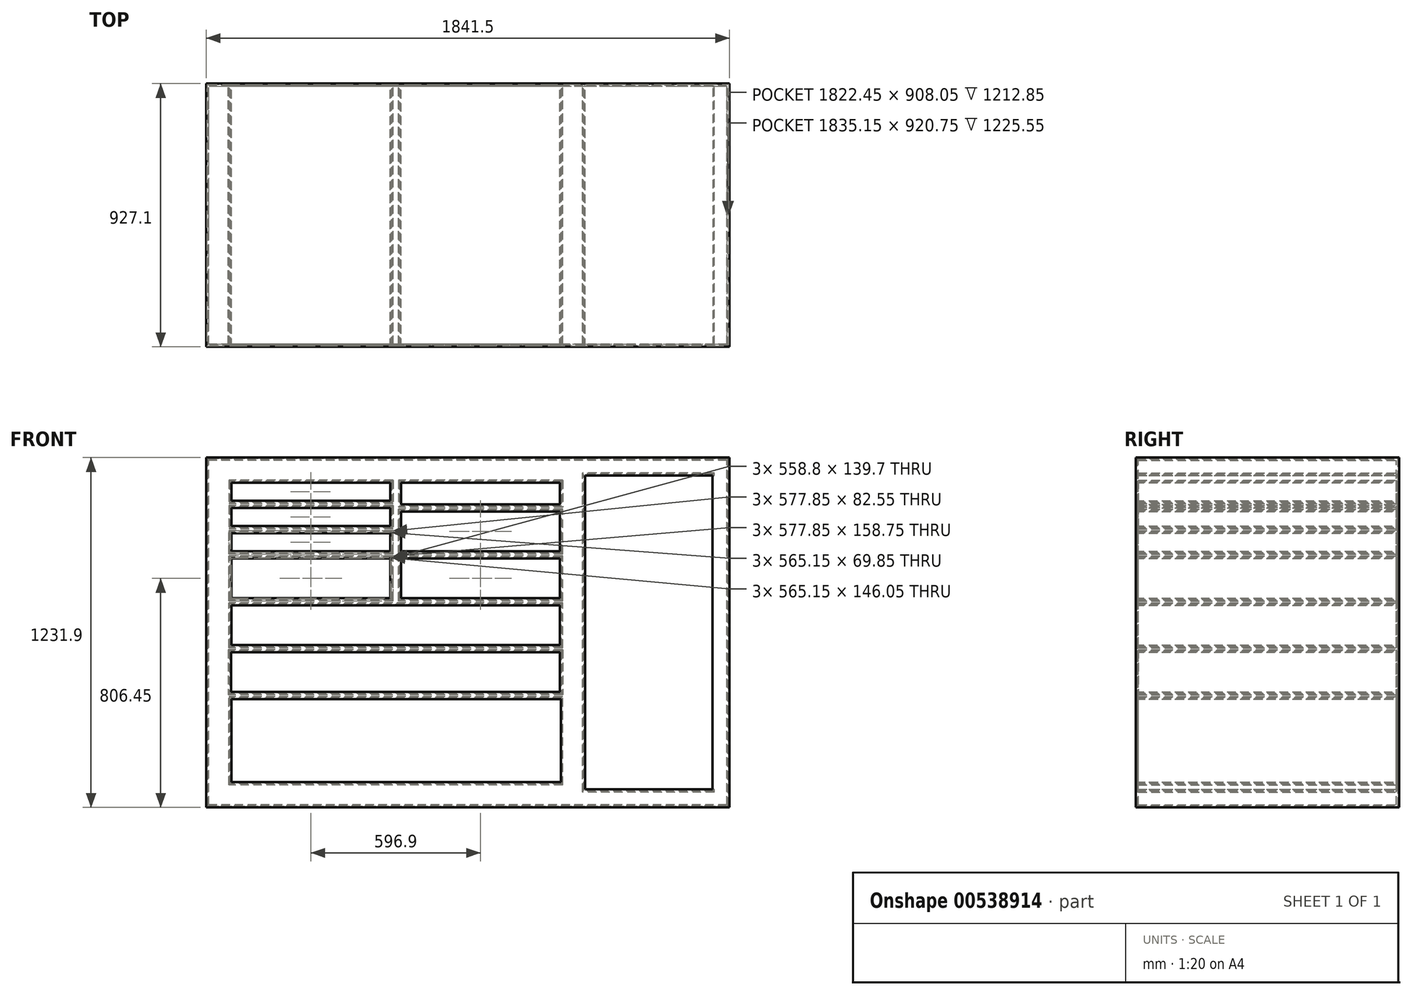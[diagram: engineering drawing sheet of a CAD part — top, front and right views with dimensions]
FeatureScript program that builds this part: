
annotation { "Feature Type Name" : "Feature", "Feature Type Description" : "" }
export const myFeature = defineFeature(function(context is Context, id is Id, definition is map)
    precondition{}
    {
        {
            var Q0;
            Q0=qCreatedBy(makeId("Front.planeOp"),FACE);
            var sketch = newSketch(context, id + "F0", { "sketchPlane" : qUnion([Q0])});
            skLineSegment(sketch, "E0.bottom", {"start": v(914.4, -609.6) * mm, "end": v(-914.4, -609.6) * mm});
            skLineSegment(sketch, "E0.top", {"start": v(914.4, 609.6) * mm, "end": v(-914.4, 609.6) * mm});
            skLineSegment(sketch, "E0.left", {"start": v(914.4, -609.6) * mm, "end": v(914.4, 609.6) * mm});
            skLineSegment(sketch, "E0.right", {"start": v(-914.4, -609.6) * mm, "end": v(-914.4, 609.6) * mm});
            skPoint(sketch, "E0.middle", {"position": v(0, 0) * mm});
            skPoint(sketch, "E1", {"position": v(635, 0) * mm});
            skLineSegment(sketch, "E2.bottom", {"start": v(863.6, -558.8) * mm, "end": v(406.4, -558.8) * mm});
            skLineSegment(sketch, "E2.top", {"start": v(863.6, 558.8) * mm, "end": v(406.4, 558.8) * mm});
            skLineSegment(sketch, "E2.left", {"start": v(863.6, -558.8) * mm, "end": v(863.6, 558.8) * mm});
            skLineSegment(sketch, "E2.right", {"start": v(406.4, -558.8) * mm, "end": v(406.4, 558.8) * mm});
            skPoint(sketch, "E3", {"position": v(-254, -381) * mm});
            skLineSegment(sketch, "E4.bottom", {"start": v(330.2, -533.4) * mm, "end": v(-838.2, -533.4) * mm});
            skLineSegment(sketch, "E4.top", {"start": v(330.2, -228.6) * mm, "end": v(-838.2, -228.6) * mm});
            skLineSegment(sketch, "E4.left", {"start": v(330.2, -533.4) * mm, "end": v(330.2, -228.6) * mm});
            skLineSegment(sketch, "E4.right", {"start": v(-838.2, -533.4) * mm, "end": v(-838.2, -228.6) * mm});
            skPoint(sketch, "E5", {"position": v(-254.77, -162.72) * mm});
            skPoint(sketch, "E6", {"position": v(-254.77, -139.7) * mm});
            skLineSegment(sketch, "E7.bottom", {"start": v(330.2, -63.5) * mm, "end": v(-839.75, -63.5) * mm});
            skLineSegment(sketch, "E7.top", {"start": v(330.2, -215.9) * mm, "end": v(-839.75, -215.9) * mm});
            skLineSegment(sketch, "E7.left", {"start": v(330.2, -63.5) * mm, "end": v(330.2, -215.9) * mm});
            skLineSegment(sketch, "E7.right", {"start": v(-839.75, -63.5) * mm, "end": v(-839.75, -215.9) * mm});
            skPoint(sketch, "E8", {"position": v(-254, 101.6) * mm});
            skPoint(sketch, "E9", {"position": v(-254, 266.7) * mm});
            skLineSegment(sketch, "E10.bottom", {"start": v(330.2, -50.8) * mm, "end": v(-838.2, -50.8) * mm});
            skLineSegment(sketch, "E10.top", {"start": v(330.2, 101.6) * mm, "end": v(-838.2, 101.6) * mm});
            skLineSegment(sketch, "E10.left", {"start": v(330.2, -50.8) * mm, "end": v(330.2, 101.6) * mm});
            skLineSegment(sketch, "E10.right", {"start": v(-838.2, -50.8) * mm, "end": v(-838.2, 101.6) * mm});
            skPoint(sketch, "E10.middle", {"position": v(-254, 78.58) * mm});
            skPoint(sketch, "E11", {"position": v(-584.2, 117.2) * mm});
            skPoint(sketch, "E12", {"position": v(44.45, 190.5) * mm});
            skPoint(sketch, "E13", {"position": v(-552.45, 317.5) * mm});
            skPoint(sketch, "E14", {"position": v(44.45, 355.6) * mm});
            skLineSegment(sketch, "E15.bottom", {"start": v(-266.7, 114.3) * mm, "end": v(-838.2, 114.3) * mm});
            skLineSegment(sketch, "E15.top", {"start": v(-266.7, 266.7) * mm, "end": v(-838.2, 266.7) * mm});
            skLineSegment(sketch, "E15.left", {"start": v(-266.7, 114.3) * mm, "end": v(-266.7, 266.7) * mm});
            skLineSegment(sketch, "E15.right", {"start": v(-838.2, 114.3) * mm, "end": v(-838.2, 266.7) * mm});
            skPoint(sketch, "E15.middle", {"position": v(-584.2, 238.8) * mm});
            skLineSegment(sketch, "E16.bottom", {"start": v(-266.7, 279.4) * mm, "end": v(-838.2, 279.4) * mm});
            skLineSegment(sketch, "E16.top", {"start": v(-266.7, 355.6) * mm, "end": v(-838.2, 355.6) * mm});
            skLineSegment(sketch, "E16.left", {"start": v(-266.7, 279.4) * mm, "end": v(-266.7, 355.6) * mm});
            skLineSegment(sketch, "E16.right", {"start": v(-838.2, 279.4) * mm, "end": v(-838.2, 355.6) * mm});
            skPoint(sketch, "E17", {"position": v(-552.45, 406.4) * mm});
            skPoint(sketch, "E17.positionSnap0", {"position": v(-552.45, 355.6) * mm});
            skLineSegment(sketch, "E18.bottom", {"start": v(-266.7, 444.5) * mm, "end": v(-838.2, 444.5) * mm});
            skLineSegment(sketch, "E18.top", {"start": v(-266.7, 368.3) * mm, "end": v(-838.2, 368.3) * mm});
            skLineSegment(sketch, "E18.left", {"start": v(-266.7, 444.5) * mm, "end": v(-266.7, 368.3) * mm});
            skLineSegment(sketch, "E18.right", {"start": v(-838.2, 444.5) * mm, "end": v(-838.2, 368.3) * mm});
            skPoint(sketch, "E19", {"position": v(-552.45, 495.3) * mm});
            skPoint(sketch, "E19.positionSnap0", {"position": v(-552.45, 444.5) * mm});
            skLineSegment(sketch, "E20.bottom", {"start": v(-266.7, 533.4) * mm, "end": v(-838.2, 533.4) * mm});
            skLineSegment(sketch, "E20.top", {"start": v(-266.7, 457.2) * mm, "end": v(-838.2, 457.2) * mm});
            skLineSegment(sketch, "E20.left", {"start": v(-266.7, 533.4) * mm, "end": v(-266.7, 457.2) * mm});
            skLineSegment(sketch, "E20.right", {"start": v(-838.2, 533.4) * mm, "end": v(-838.2, 457.2) * mm});
            skLineSegment(sketch, "E21.bottom", {"start": v(330.2, 114.3) * mm, "end": v(-241.3, 114.3) * mm});
            skLineSegment(sketch, "E21.top", {"start": v(330.2, 266.7) * mm, "end": v(-241.3, 266.7) * mm});
            skLineSegment(sketch, "E21.left", {"start": v(330.2, 114.3) * mm, "end": v(330.2, 266.7) * mm});
            skLineSegment(sketch, "E21.right", {"start": v(-241.3, 114.3) * mm, "end": v(-241.3, 266.7) * mm});
            skLineSegment(sketch, "E22.bottom", {"start": v(330.2, 279.4) * mm, "end": v(-241.3, 279.4) * mm});
            skLineSegment(sketch, "E22.top", {"start": v(330.2, 431.8) * mm, "end": v(-241.3, 431.8) * mm});
            skLineSegment(sketch, "E22.left", {"start": v(330.2, 279.4) * mm, "end": v(330.2, 431.8) * mm});
            skLineSegment(sketch, "E22.right", {"start": v(-241.3, 279.4) * mm, "end": v(-241.3, 431.8) * mm});
            skPoint(sketch, "E23", {"position": v(44.45, 488.95) * mm});
            skLineSegment(sketch, "E24.bottom", {"start": v(330.2, 533.4) * mm, "end": v(-241.3, 533.4) * mm});
            skLineSegment(sketch, "E24.top", {"start": v(330.2, 444.5) * mm, "end": v(-241.3, 444.5) * mm});
            skLineSegment(sketch, "E24.left", {"start": v(330.2, 533.4) * mm, "end": v(330.2, 444.5) * mm});
            skLineSegment(sketch, "E24.right", {"start": v(-241.3, 533.4) * mm, "end": v(-241.3, 444.5) * mm});
            skSolve(sketch);
        }
        {
            var Q0;
            Q0=makeQuery(id+"F0.imprint","IMPRINT",FACE,{"disambiguationData":[TD([[makeQuery(id+"F0.imprint","IMPRINT",EDGE,{"derivedFrom":sQuery(id+"F0.wireOp",EDGE,"E0.bottom")}),-1.0]])]});
            extrude(context, id + "F1", {"entities" : qUnion([Q0]), "depth" : 914.4 * mm, "offsetDistance" : 25.4 * mm});
        }
        {
            var Q0;
            Q0=makeQuery(id+"F1.opExtrude","SWEPT_FACE",FACE,{"disambiguationData":[OSD([sQuery(id+"F0.wireOp",EDGE,"E2.left")])]});
            shell(context, id + "F2", {"entities" : qUnion([Q0]), "thickness" : 3.17 * mm, "oppositeDirection" : true});
        }
        {
            var Q0;
            Q0=makeQuery(id+"F1.opExtrude","SWEPT_FACE",FACE,{"disambiguationData":[OSD([sQuery(id+"F0.wireOp",EDGE,"E4.left")])]});
            shell(context, id + "F3", {"entities" : qUnion([Q0]), "thickness" : 3.17 * mm, "oppositeDirection" : true});
        }
        {
            var Q0;
            Q0=qCreatedBy(makeId("Front.planeOp"),FACE);
            var sketch = newSketch(context, id + "F4", { "sketchPlane" : qUnion([Q0])});
            skLineSegment(sketch, "E25.bottom", {"start": v(-914.4, -609.6) * mm, "end": v(914.4, -609.6) * mm});
            skLineSegment(sketch, "E25.top", {"start": v(-914.4, 609.6) * mm, "end": v(914.4, 609.6) * mm});
            skLineSegment(sketch, "E25.left", {"start": v(-914.4, -609.6) * mm, "end": v(-914.4, 609.6) * mm});
            skLineSegment(sketch, "E25.right", {"start": v(914.4, -609.6) * mm, "end": v(914.4, 609.6) * mm});
            skPoint(sketch, "E25.middle", {"position": v(0, 0) * mm});
            skSolve(sketch);
        }
        {
            var Q0;
            Q0=makeQuery(id+"F4.imprint","IMPRINT",FACE,{"disambiguationData":[TD([[makeQuery(id+"F4.imprint","IMPRINT",EDGE,{"derivedFrom":sQuery(id+"F4.wireOp",EDGE,"E25.bottom")}),1.0]])]});
            var Q1;
            Q1=sQuery(id+"F4.wireOp",EDGE,"E25.bottom");
            var Q2;
            Q2=sQuery(id+"F4.wireOp",EDGE,"E25.top");
            var Q3;
            Q3=sQuery(id+"F4.wireOp",EDGE,"E25.right");
            var Q4;
            Q4=sQuery(id+"F4.wireOp",EDGE,"E25.left");
            extrude(context, id + "F5", {"entities" : qUnion([Q0]), "operationType" : NewBodyOperationType.ADD, "surfaceEntities" : qUnion([Q1, Q2, Q3, Q4]), "oppositeDirection" : true, "depth" : 3.17 * mm, "offsetDistance" : 25.4 * mm});
        }
    });
